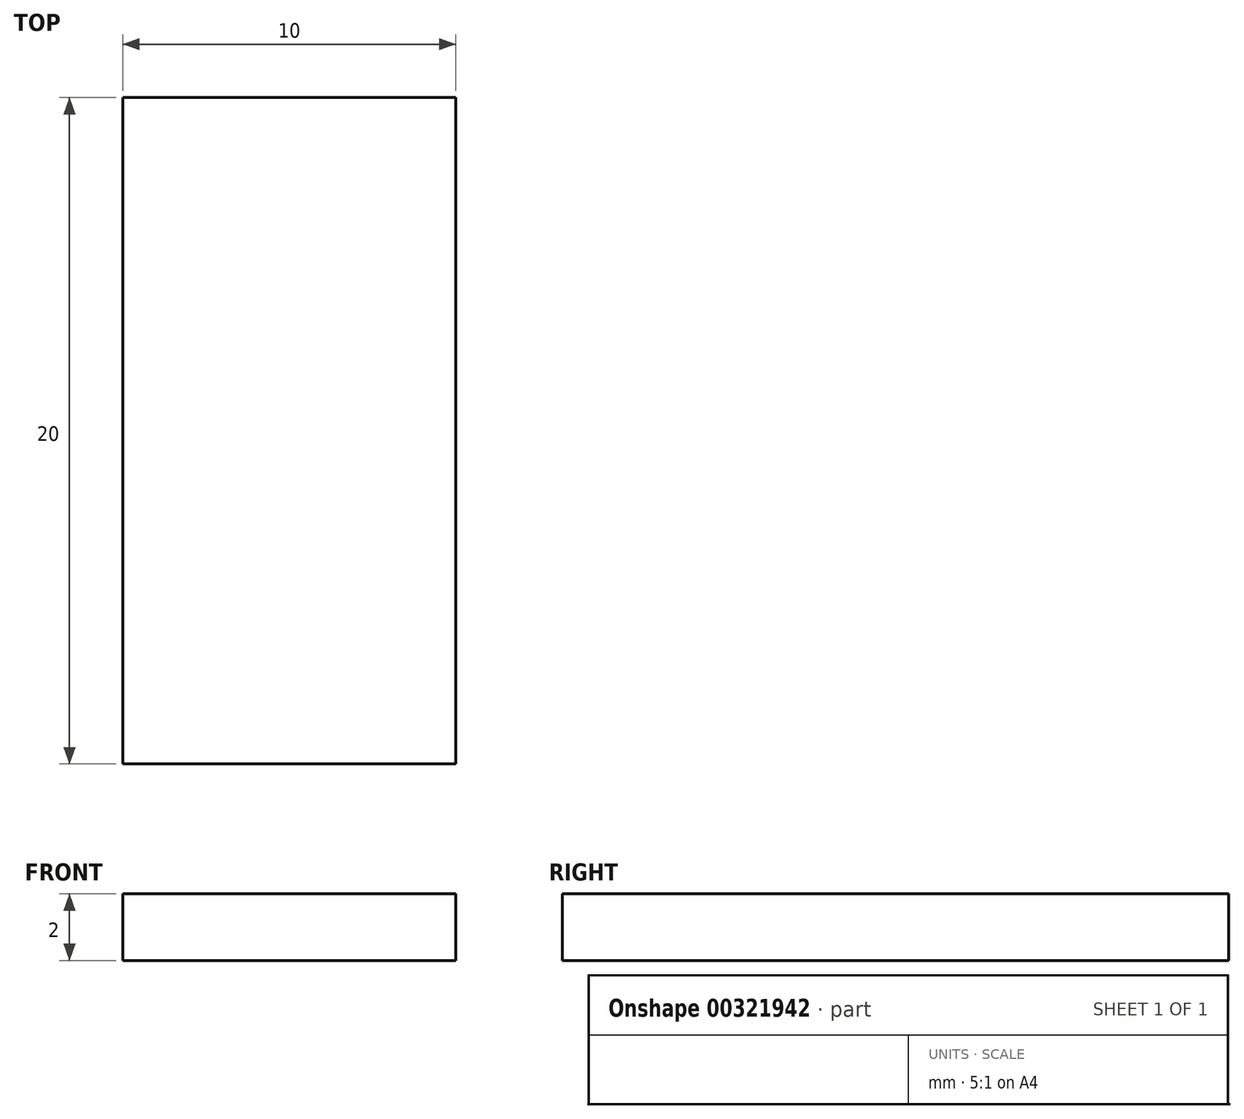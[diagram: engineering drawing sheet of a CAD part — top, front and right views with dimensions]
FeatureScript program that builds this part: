
annotation { "Feature Type Name" : "Feature", "Feature Type Description" : "" }
export const myFeature = defineFeature(function(context is Context, id is Id, definition is map)
    precondition{}
    {
        {
            var Q0;
            Q0=qCreatedBy(makeId("Top.planeOp"),FACE);
            var sketch = newSketch(context, id + "F0", { "sketchPlane" : qUnion([Q0])});
            skLineSegment(sketch, "E0.bottom", {"start": v(5, 10) * mm, "end": v(-5, 10) * mm});
            skLineSegment(sketch, "E0.top", {"start": v(5, -10) * mm, "end": v(-5, -10) * mm});
            skLineSegment(sketch, "E0.left", {"start": v(5, 10) * mm, "end": v(5, -10) * mm});
            skLineSegment(sketch, "E0.right", {"start": v(-5, 10) * mm, "end": v(-5, -10) * mm});
            skPoint(sketch, "E0.middle", {"position": v(0, 0) * mm});
            skSolve(sketch);
        }
        {
            var Q0;
            Q0 = qSketchRegion(id + "F0", true);
            extrude(context, id + "F1", {"entities" : qUnion([Q0]), "endBound" : BoundingType.SYMMETRIC, "depth" : 2 * mm});
        }
    });
